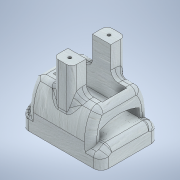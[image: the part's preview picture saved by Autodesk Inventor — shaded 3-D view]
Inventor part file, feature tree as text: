
AUTODESK INVENTOR PART (.ipt)
format: ipt  version: 2021 (Build 250183000, 183)  size: 1,119,744 bytes
history: native  units: mm
features: extrude x21, sketch x21, fillet x7, projected_geometry x7, plane x1, mirror x1
ambient origin geometry x8: Origin, YZ Plane, XZ Plane, XY Plane, X Axis, Y Axis, Z Axis, Center Point
bodies: Solid1 (feature_tree)
feature tree (58):
  extrude  "Extrusion1"  Depth=39.0mm
  extrude  "Extrusion2"  Depth=8.0mm
  plane  "Work Plane2"
  mirror  "Mirror1"
  extrude  "Extrusion3"  Depth=8.0mm
  extrude  "Extrusion4"  Depth=4.0mm TaperAngle=0.0deg
  extrude  "Extrusion5"  Depth=27.0mm
  extrude  "Extrusion6"  Depth=4.0mm TaperAngle=0.0deg
  extrude  "Extrusion7"  Depth=19.0mm
  extrude  "Extrusion8"  Depth=4.0mm TaperAngle=0.0deg
  extrude  "Extrusion9"  Depth=4.0mm TaperAngle=0.0deg
  extrude  "Extrusion10"  Depth=2.0mm TaperAngle=0.0deg
  extrude  "Extrusion11"  Depth=12.5mm
  extrude  "Extrusion12"  Depth=4.0mm
  extrude  "Extrusion13"  Depth=7.9mm
  extrude  "Extrusion14"  Depth=7.9mm
  extrude  "Extrusion15"  Depth=15.0mm TaperAngle=0.0deg
  extrude  "Extrusion16"  Depth=8.5mm TaperAngle=0.0deg
  extrude  "Extrusion17"  Depth=8.5mm TaperAngle=0.0deg
  fillet  "Fillet6"  Radius=36.0mm
  fillet  "Fillet7"  Radius=8.5mm
  fillet  "Fillet8"  Radius=15.0mm
  extrude  "Extrusion18"  Depth=6.0mm
  fillet  "Fillet9"  Radius=6.0mm
  fillet  "Fillet10"  Radius=30.0mm
  extrude  "Extrusion19"  Depth=3.0mm
  fillet  "Fillet12"  Radius=5.0mm
  fillet  "Fillet13"  Radius=5.0mm
  extrude  "Extrusion20"  Depth=3.0mm
  extrude  "Extrusion21"  Depth=10.0mm
  sketch  "Sketch1"  dims[d0=15.0mm d1=39.0mm]
  sketch  "Sketch2"  dims[d2=4.0mm d3=0.0mm d5=8.0mm]
  sketch  "Sketch3"  dims[d6=15.0mm d7=8.0mm]
  sketch  "Sketch4"  dims[d8=14.0mm d9=4.0mm d10=0.0mm]
  sketch  "Sketch5"  dims[d12=10.0mm d13=27.0mm]
  sketch  "Sketch7"  dims[d14=28.0mm d15=4.0mm d16=0.0mm]
  sketch  "Sketch8"  dims[d17=28.0mm d18=19.0mm]
  sketch  "Sketch10"  dims[d19=4.0mm d20=0.0mm d21=4.0mm d22=0.0mm]
  projected_geometry  "Projected Loop2"
  sketch  "Sketch11"  dims[d23=13.0mm d24=0.0mm d25=4.0mm d26=0.0mm]
  projected_geometry  "Projected Loop3"
  sketch  "Sketch12"  dims[d27=3.0mm d28=0.0mm d29=2.0mm d30=0.0mm]
  projected_geometry  "Projected Loop4"
  sketch  "Sketch14"  dims[d31=2.0mm d32=0.0mm d35=12.5mm]
  sketch  "Sketch15"  dims[d36=11.5mm d37=4.0mm]
  sketch  "Sketch18"  dims[d38=6.0mm d39=7.9mm]
  sketch  "Sketch19"  dims[d40=7.9mm d41=7.9mm]
  projected_geometry  "Projected Loop9"
  sketch  "Sketch20"  dims[d42=7.9mm d43=15.0mm d44=0.0mm]
  projected_geometry  "Projected Loop10"
  sketch  "Sketch21"  dims[d45=0.2mm d46=0.0mm d49=8.5mm d50=56.5mm d51=0.0mm d52=0.0mm]
  sketch  "Sketch22"  dims[d53=8.5mm d54=0.0mm d55=8.5mm d56=0.0mm d57=36.0mm d58=8.5mm d59=0.0mm d61=15.0mm d62=0.0mm]
  sketch  "Sketch23"  dims[d63=4.0mm d64=6.0mm d65=6.0mm d66=30.0mm]
  sketch  "Sketch24"  dims[d70=8.5mm d71=0.0mm d72=3.0mm d73=5.0mm d75=5.0mm d76=0.0mm]
  projected_geometry  "Projected Loop11"
  projected_geometry  "Projected Loop12"
  sketch  "Sketch25"  dims[d77=5.0mm d78=3.0mm]
  sketch  "Sketch26"  dims[d79=7.9mm d80=7.9mm d81=7.9mm d82=7.9mm d83=11.0mm d84=11.0mm d85=11.0mm d86=11.0mm d88=11.0mm d89=11.0mm d90=11.0mm d91=11.0mm d92=2.4mm d93=2.4mm d94=15.0mm d95=0.0mm d96=1.5mm d97=1.5mm d98=10.0mm d99=0.0mm]
